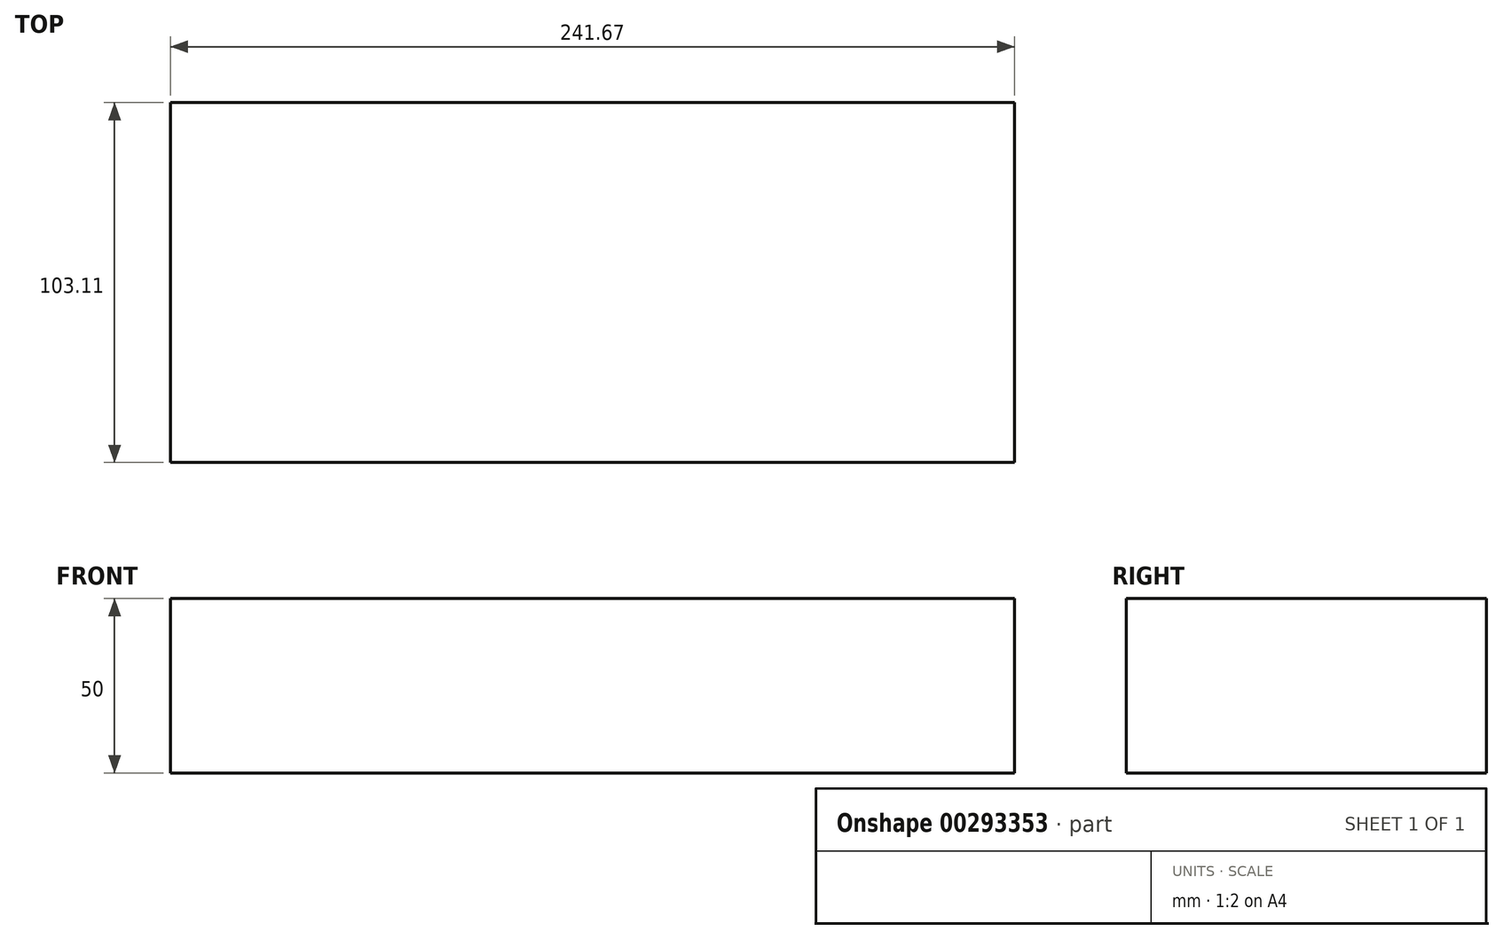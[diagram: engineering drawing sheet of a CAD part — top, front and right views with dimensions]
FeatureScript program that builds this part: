
annotation { "Feature Type Name" : "Feature", "Feature Type Description" : "" }
export const myFeature = defineFeature(function(context is Context, id is Id, definition is map)
    precondition{}
    {
        {
            var Q0;
            Q0=qCreatedBy(makeId("Top.planeOp"),FACE);
            var sketch = newSketch(context, id + "F0", { "sketchPlane" : qUnion([Q0])});
            skLineSegment(sketch, "E0.bottom", {"start": v(-117.32, 41.35) * mm, "end": v(124.35, 41.35) * mm});
            skLineSegment(sketch, "E0.top", {"start": v(-117.32, -61.76) * mm, "end": v(124.35, -61.76) * mm});
            skLineSegment(sketch, "E0.left", {"start": v(-117.32, 41.35) * mm, "end": v(-117.32, -61.76) * mm});
            skLineSegment(sketch, "E0.right", {"start": v(124.35, 41.35) * mm, "end": v(124.35, -61.76) * mm});
            skSolve(sketch);
        }
        {
            var Q0;
            Q0=makeQuery(id+"F0.imprint","IMPRINT",FACE,{"disambiguationData":[TD([[makeQuery(id+"F0.imprint","IMPRINT",EDGE,{"derivedFrom":sQuery(id+"F0.wireOp",EDGE,"E0.bottom")}),-1.0]])]});
            extrude(context, id + "F1", {"entities" : qUnion([Q0]), "depth" : 50 * mm});
        }
    });
